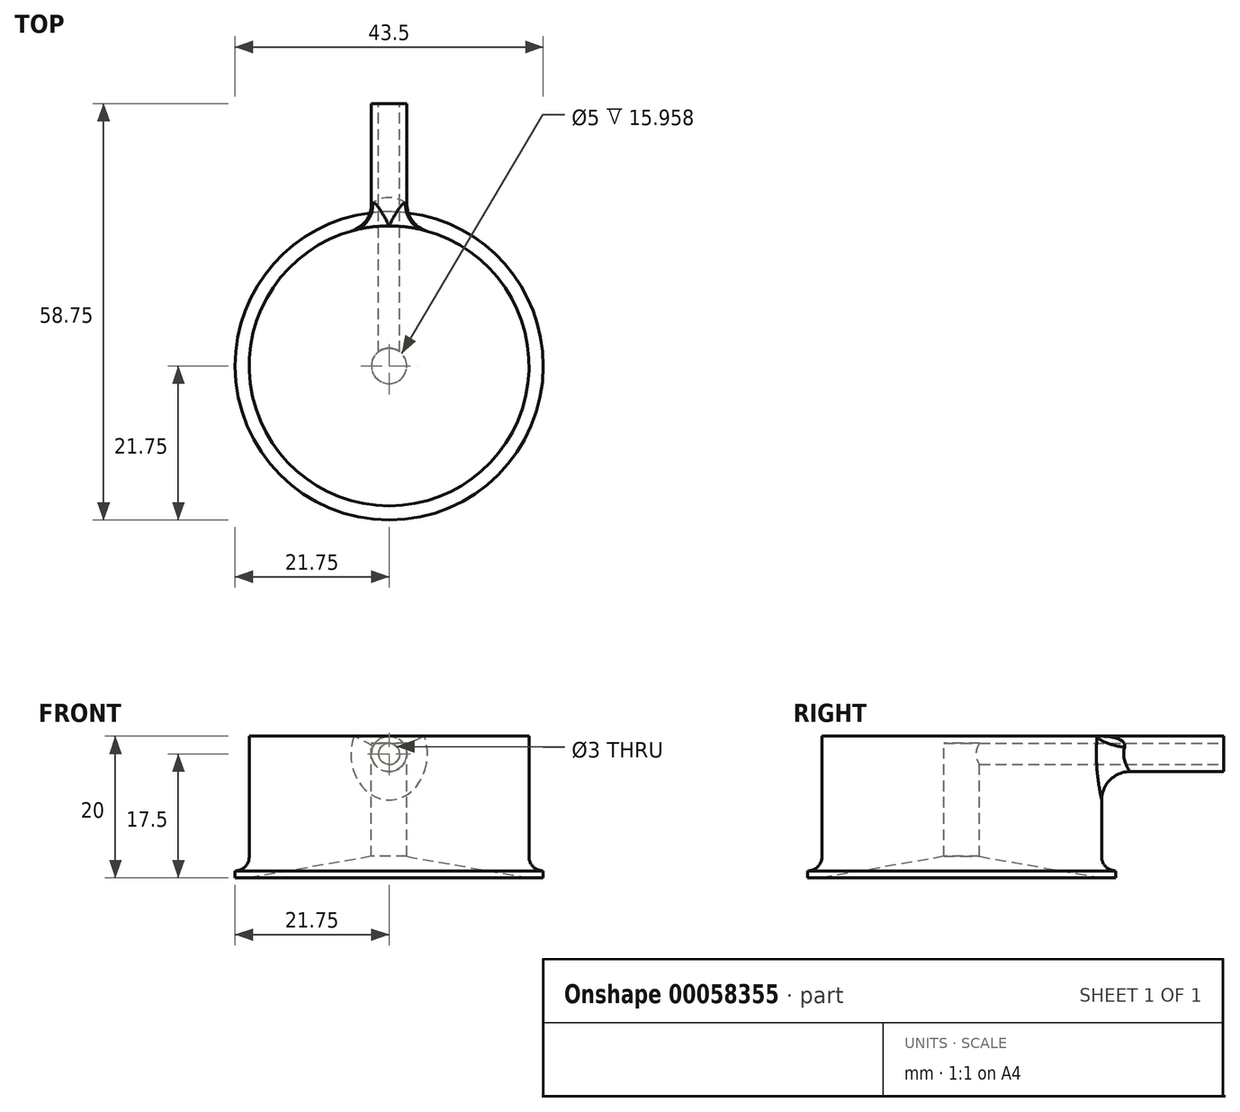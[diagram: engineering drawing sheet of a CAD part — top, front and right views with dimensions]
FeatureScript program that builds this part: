
annotation { "Feature Type Name" : "Feature", "Feature Type Description" : "" }
export const myFeature = defineFeature(function(context is Context, id is Id, definition is map)
    precondition{}
    {
        {
            var Q0;
            Q0=qCreatedBy(makeId("Front.planeOp"),FACE);
            var sketch = newSketch(context, id + "F0", { "sketchPlane" : qUnion([Q0])});
            skLineSegment(sketch, "E0", {"start": v(0, 0) * mm, "end": v(-21.75, 0) * mm, "construction": true});
            skLineSegment(sketch, "E1", {"start": v(-21.75, 0) * mm, "end": v(-21.75, 1) * mm, "construction": true});
            skLineSegment(sketch, "E2", {"start": v(-21.75, 1) * mm, "end": v(-19.75, 1) * mm, "construction": true});
            skLineSegment(sketch, "E3", {"start": v(-19.75, 1) * mm, "end": v(-19.75, 3.5) * mm, "construction": true});
            skLineSegment(sketch, "E4", {"start": v(-2.5, 0) * mm, "end": v(-2.5, 20) * mm, "construction": true});
            skLineSegment(sketch, "E5", {"start": v(0, 20) * mm, "end": v(-2.5, 20) * mm, "construction": true});
            skLineSegment(sketch, "E6", {"start": v(-2.5, 20) * mm, "end": v(-19.75, 20) * mm, "construction": true});
            skLineSegment(sketch, "E7", {"start": v(-19.75, 20) * mm, "end": v(-19.75, 3.5) * mm, "construction": true});
            skLineSegment(sketch, "E8", {"start": v(-19.75, 1) * mm, "end": v(-19.75, 0) * mm, "construction": true});
            skLineSegment(sketch, "E9", {"start": v(-19.75, 0) * mm, "end": v(-2.5, 3.04) * mm, "construction": true});
            skLineSegment(sketch, "E10", {"start": v(0, 20) * mm, "end": v(0, 0) * mm, "construction": true});
            skLineSegment(sketch, "E11", {"start": v(-2.5, 3.04) * mm, "end": v(0, 3.04) * mm, "construction": true});
            skLineSegment(sketch, "E12", {"start": v(-2.5, 3.04) * mm, "end": v(-19.75, 0) * mm});
            skLineSegment(sketch, "E13", {"start": v(-19.75, 0) * mm, "end": v(-21.75, 0) * mm});
            skLineSegment(sketch, "E14", {"start": v(-21.75, 0) * mm, "end": v(-21.75, 1) * mm});
            skLineSegment(sketch, "E15", {"start": v(-21.75, 1) * mm, "end": v(-19.75, 1) * mm});
            skLineSegment(sketch, "E16", {"start": v(-19.75, 1) * mm, "end": v(-19.75, 20) * mm});
            skLineSegment(sketch, "E17", {"start": v(-19.75, 20) * mm, "end": v(-2.5, 20) * mm});
            skLineSegment(sketch, "E18", {"start": v(-2.5, 19) * mm, "end": v(0, 19) * mm, "construction": true});
            skLineSegment(sketch, "E19", {"start": v(-2.5, 3.04) * mm, "end": v(-2.5, 19) * mm});
            skLineSegment(sketch, "E20", {"start": v(-2.5, 19) * mm, "end": v(0, 19) * mm});
            skLineSegment(sketch, "E21", {"start": v(0, 19) * mm, "end": v(0, 20) * mm});
            skLineSegment(sketch, "E22", {"start": v(0, 20) * mm, "end": v(-2.5, 20) * mm});
            skSolve(sketch);
        }
        {
            var Q0;
            Q0=makeQuery(id+"F0.imprint","IMPRINT",FACE,{"disambiguationData":[TD([[makeQuery(id+"F0.imprint","IMPRINT",EDGE,{"derivedFrom":sQuery(id+"F0.wireOp",EDGE,"E12")}),-1.0]])]});
            var Q1;
            {var subQ0=sQuery(id+"F0.wireOp",EDGE,"E15");Q1=makeQuery(id+"F0.imprint","IMPRINT",FACE,{"disambiguationData":[TD([[makeQuery(id+"F0.imprint","IMPRINT",EDGE,{"derivedFrom":subQ0}),1.0]])]});}
            var Q2;
            Q2=sQuery(id+"F0.wireOp",EDGE,"E10");
            revolve(context, id + "F1", {"entities" : qUnion([Q0, Q1]), "axis" : qUnion([Q2]), "revolveType" : RevolveType.FULL});
        }
        {
            var Q0;
            Q0=qCreatedBy(makeId("Front.planeOp"),FACE);
            cPlane(context, id + "F2", {"entities" : qUnion([Q0]), "cplaneType" : CPlaneType.OFFSET, "offset" : 22 * mm, "oppositeDirection" : true, "width" : 150 * mm, "height" : 150 * mm});
        }
        {
            var Q0;
            Q0=qCreatedBy(id+"F2.planeOp",FACE);
            var sketch = newSketch(context, id + "F3", { "sketchPlane" : qUnion([Q0])});
            skCircle(sketch, "E23", {"center": v(0, 17.5) * mm, "radius": 2.5 * mm});
            skCircle(sketch, "E24", {"center": v(0, 17.5) * mm, "radius": 1.5 * mm});
            skSolve(sketch);
        }
        {
            var Q0;
            Q0=qSketchRegion(id+"F3",true);
            var Q1;
            Q1=makeQuery(id+"F1.opRevolve","SWEPT_FACE",FACE,{"disambiguationData":[OSD([sQuery(id+"F0.wireOp",EDGE,"E16")])]});
            extrude(context, id + "F4", {"entities" : qUnion([Q0]), "operationType" : NewBodyOperationType.ADD, "endBound" : BoundingType.UP_TO_SURFACE, "endBoundEntityFace" : qUnion([Q1]), "depth" : 25 * mm, "hasSecondDirection" : true, "secondDirectionOppositeDirection" : true, "secondDirectionDepth" : 15 * mm});
        }
        {
            var Q0;
            Q0=makeQuery(id+"F3.imprint","IMPRINT",FACE,{"disambiguationData":[TD([[makeQuery(id+"F3.imprint","IMPRINT",EDGE,{"derivedFrom":sQuery(id+"F3.wireOp",EDGE,"E24")}),1.0]])]});
            extrude(context, id + "F5", {"entities" : qUnion([Q0]), "operationType" : NewBodyOperationType.REMOVE, "depth" : 22.5 * mm});
        }
        {
            var Q0;
            Q0=makeQuery(id+"F4.opExtrude","CAP_EDGE",EDGE,{"disambiguationData":[OSD([sQuery(id+"F3.wireOp",EDGE,"E23")])],"isStart":false});
            fillet(context, id + "F6", {"entities" : qUnion([Q0]), "radius" : 4 * mm, "tangentPropagation" : true, "allowEdgeOverflow" : false});
        }
        {
            var Q0;
            Q0=makeQuery(id+"F1.opRevolve","SWEPT_EDGE",EDGE,{"disambiguationData":[OSD([sQuery(id+"F0.wireOp",EDGE,"E15"),sQuery(id+"F0.wireOp",EDGE,"E16")])]});
            fillet(context, id + "F7", {"entities" : qUnion([Q0]), "radius" : 2 * mm, "tangentPropagation" : true, "allowEdgeOverflow" : false});
        }
    });
